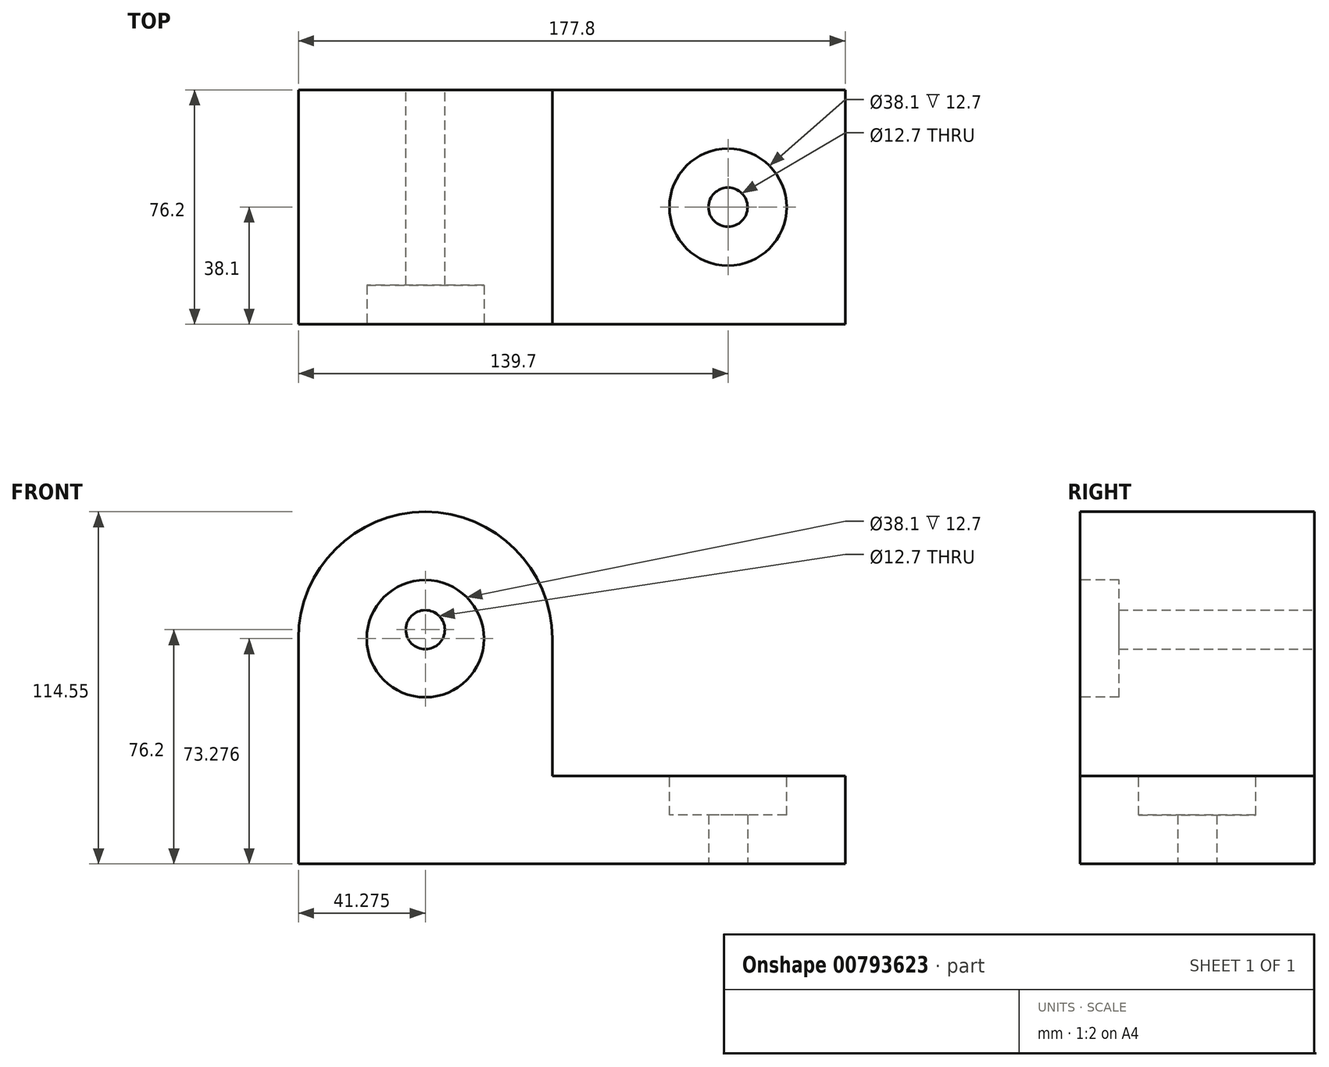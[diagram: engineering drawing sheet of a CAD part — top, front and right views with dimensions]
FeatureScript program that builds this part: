
annotation { "Feature Type Name" : "Feature", "Feature Type Description" : "" }
export const myFeature = defineFeature(function(context is Context, id is Id, definition is map)
    precondition{}
    {
        {
            var Q0;
            Q0=qCreatedBy(makeId("Front.planeOp"),FACE);
            var sketch = newSketch(context, id + "F0", { "sketchPlane" : qUnion([Q0])});
            skLineSegment(sketch, "E0", {"start": v(0, 0) * mm, "end": v(177.8, 0) * mm});
            skLineSegment(sketch, "E1", {"start": v(177.8, 0) * mm, "end": v(177.8, 28.58) * mm});
            skLineSegment(sketch, "E2", {"start": v(177.8, 28.58) * mm, "end": v(82.55, 28.58) * mm});
            skLineSegment(sketch, "E3", {"start": v(0, 0) * mm, "end": v(0, 127) * mm});
            skLineSegment(sketch, "E4", {"start": v(0, 127) * mm, "end": v(82.55, 127) * mm});
            skLineSegment(sketch, "E5", {"start": v(82.55, 127) * mm, "end": v(82.55, 28.58) * mm});
            skSolve(sketch);
        }
        {
            var Q0;
            Q0=makeQuery(id+"F0.imprint","IMPRINT",FACE,{"disambiguationData":[TD([[makeQuery(id+"F0.imprint","IMPRINT",EDGE,{"derivedFrom":sQuery(id+"F0.wireOp",EDGE,"E0")}),1.0]])]});
            extrude(context, id + "F1", {"entities" : qUnion([Q0]), "depth" : 76.2 * mm, "offsetDistance" : 25.4 * mm});
        }
        {
            var Q0;
            Q0=makeQuery(id+"F1.opExtrude","CAP_FACE",FACE,{"disambiguationData":[OSD([sQuery(id+"F0.wireOp",EDGE,"E0"),sQuery(id+"F0.wireOp",EDGE,"E1"),sQuery(id+"F0.wireOp",EDGE,"E2"),sQuery(id+"F0.wireOp",EDGE,"E3"),sQuery(id+"F0.wireOp",EDGE,"E4"),sQuery(id+"F0.wireOp",EDGE,"E5")])],"isStart":false});
            var sketch = newSketch(context, id + "F2", { "sketchPlane" : qUnion([Q0])});
            skLineSegment(sketch, "E6", {"start": v(0, -2.92) * mm, "end": v(0, 73.28) * mm, "construction": true});
            skLineSegment(sketch, "E7", {"start": v(0, 73.28) * mm, "end": v(82.55, 73.28) * mm, "construction": true});
            skLineSegment(sketch, "E8", {"start": v(41.28, 73.28) * mm, "end": v(41.28, 114.55) * mm, "construction": true});
            skArc(sketch, "E9", {"start": v(82.55, 73.28) * mm, "mid": v(41.27, 114.55) * mm, "end": v(0, 73.28) * mm});
            skSolve(sketch);
        }
        {
            var Q0;
            {var subQ0=sQuery(id+"F2.wireOp",EDGE,"E9");Q0=makeQuery(id+"F2.imprint","IMPRINT",FACE,{"disambiguationData":[TD([[makeQuery(id+"F2.imprint","IMPRINT",EDGE,{"derivedFrom":subQ0}),-1.0]])]});}
            extrude(context, id + "F3", {"entities" : qUnion([Q0]), "operationType" : NewBodyOperationType.REMOVE, "endBound" : BoundingType.THROUGH_ALL, "oppositeDirection" : true, "depth" : 25.4 * mm, "offsetDistance" : 25.4 * mm});
        }
        {
            var Q0;
            Q0=makeQuery(id+"F1.opExtrude","CAP_FACE",FACE,{"disambiguationData":[OSD([sQuery(id+"F0.wireOp",EDGE,"E0"),sQuery(id+"F0.wireOp",EDGE,"E1"),sQuery(id+"F0.wireOp",EDGE,"E2"),sQuery(id+"F0.wireOp",EDGE,"E3"),sQuery(id+"F0.wireOp",EDGE,"E4"),sQuery(id+"F0.wireOp",EDGE,"E5")])],"isStart":false});
            var sketch = newSketch(context, id + "F4", { "sketchPlane" : qUnion([Q0])});
            skLineSegment(sketch, "E10", {"start": v(41.27, 114.55) * mm, "end": v(41.27, 73.28) * mm, "construction": true});
            skCircle(sketch, "E11", {"center": v(41.27, 73.28) * mm, "radius": 19.05 * mm});
            skSolve(sketch);
        }
        {
            var Q0;
            Q0=makeQuery(id+"F4.imprint","IMPRINT",FACE,{"disambiguationData":[TD([[makeQuery(id+"F4.imprint","IMPRINT",EDGE,{"derivedFrom":sQuery(id+"F4.wireOp",EDGE,"E11")}),1.0]])]});
            extrude(context, id + "F5", {"entities" : qUnion([Q0]), "operationType" : NewBodyOperationType.REMOVE, "oppositeDirection" : true, "depth" : 12.7 * mm, "offsetDistance" : 25.4 * mm});
        }
        {
            var Q0;
            Q0=makeQuery(id+"F1.opExtrude","CAP_FACE",FACE,{"disambiguationData":[OSD([sQuery(id+"F0.wireOp",EDGE,"E0"),sQuery(id+"F0.wireOp",EDGE,"E1"),sQuery(id+"F0.wireOp",EDGE,"E2"),sQuery(id+"F0.wireOp",EDGE,"E3"),sQuery(id+"F0.wireOp",EDGE,"E4"),sQuery(id+"F0.wireOp",EDGE,"E5")])],"isStart":true});
            var sketch = newSketch(context, id + "F6", { "sketchPlane" : qUnion([Q0])});
            skLineSegment(sketch, "E12", {"start": v(0, 0) * mm, "end": v(0, 76.2) * mm, "construction": true});
            skLineSegment(sketch, "E13", {"start": v(0, 76.2) * mm, "end": v(-41.28, 76.2) * mm, "construction": true});
            skCircle(sketch, "E14", {"center": v(-41.28, 76.2) * mm, "radius": 6.35 * mm});
            skSolve(sketch);
        }
        {
            var Q0;
            Q0=makeQuery(id+"F6.imprint","IMPRINT",FACE,{"disambiguationData":[TD([[makeQuery(id+"F6.imprint","IMPRINT",EDGE,{"derivedFrom":sQuery(id+"F6.wireOp",EDGE,"E14")}),1.0]])]});
            extrude(context, id + "F7", {"entities" : qUnion([Q0]), "operationType" : NewBodyOperationType.REMOVE, "endBound" : BoundingType.THROUGH_ALL, "oppositeDirection" : true, "depth" : 25.4 * mm, "offsetDistance" : 25.4 * mm});
        }
        {
            var Q0;
            Q0=makeQuery(id+"F1.opExtrude","SWEPT_FACE",FACE,{"disambiguationData":[OSD([sQuery(id+"F0.wireOp",EDGE,"E2")])]});
            var sketch = newSketch(context, id + "F8", { "sketchPlane" : qUnion([Q0])});
            skLineSegment(sketch, "E15", {"start": v(177.8, -38.1) * mm, "end": v(139.7, -38.1) * mm, "construction": true});
            skCircle(sketch, "E16", {"center": v(139.7, -38.1) * mm, "radius": 19.05 * mm});
            skSolve(sketch);
        }
        {
            var Q0;
            Q0=makeQuery(id+"F8.imprint","IMPRINT",FACE,{"disambiguationData":[TD([[makeQuery(id+"F8.imprint","IMPRINT",EDGE,{"derivedFrom":sQuery(id+"F8.wireOp",EDGE,"E16")}),1.0]])]});
            extrude(context, id + "F9", {"entities" : qUnion([Q0]), "operationType" : NewBodyOperationType.REMOVE, "oppositeDirection" : true, "depth" : 12.7 * mm, "offsetDistance" : 25.4 * mm});
        }
        {
            var Q0;
            Q0=makeQuery(id+"F1.opExtrude","SWEPT_FACE",FACE,{"disambiguationData":[OSD([sQuery(id+"F0.wireOp",EDGE,"E0")])]});
            var sketch = newSketch(context, id + "F10", { "sketchPlane" : qUnion([Q0])});
            skLineSegment(sketch, "E17", {"start": v(177.8, 38.1) * mm, "end": v(139.7, 38.1) * mm, "construction": true});
            skCircle(sketch, "E18", {"center": v(139.7, 38.1) * mm, "radius": 6.35 * mm});
            skSolve(sketch);
        }
        {
            var Q0;
            Q0=makeQuery(id+"F10.imprint","IMPRINT",FACE,{"disambiguationData":[TD([[makeQuery(id+"F10.imprint","IMPRINT",EDGE,{"derivedFrom":sQuery(id+"F10.wireOp",EDGE,"E18")}),1.0]])]});
            extrude(context, id + "F11", {"entities" : qUnion([Q0]), "operationType" : NewBodyOperationType.REMOVE, "endBound" : BoundingType.THROUGH_ALL, "oppositeDirection" : true, "depth" : 25.4 * mm, "offsetDistance" : 25.4 * mm});
        }
    });
